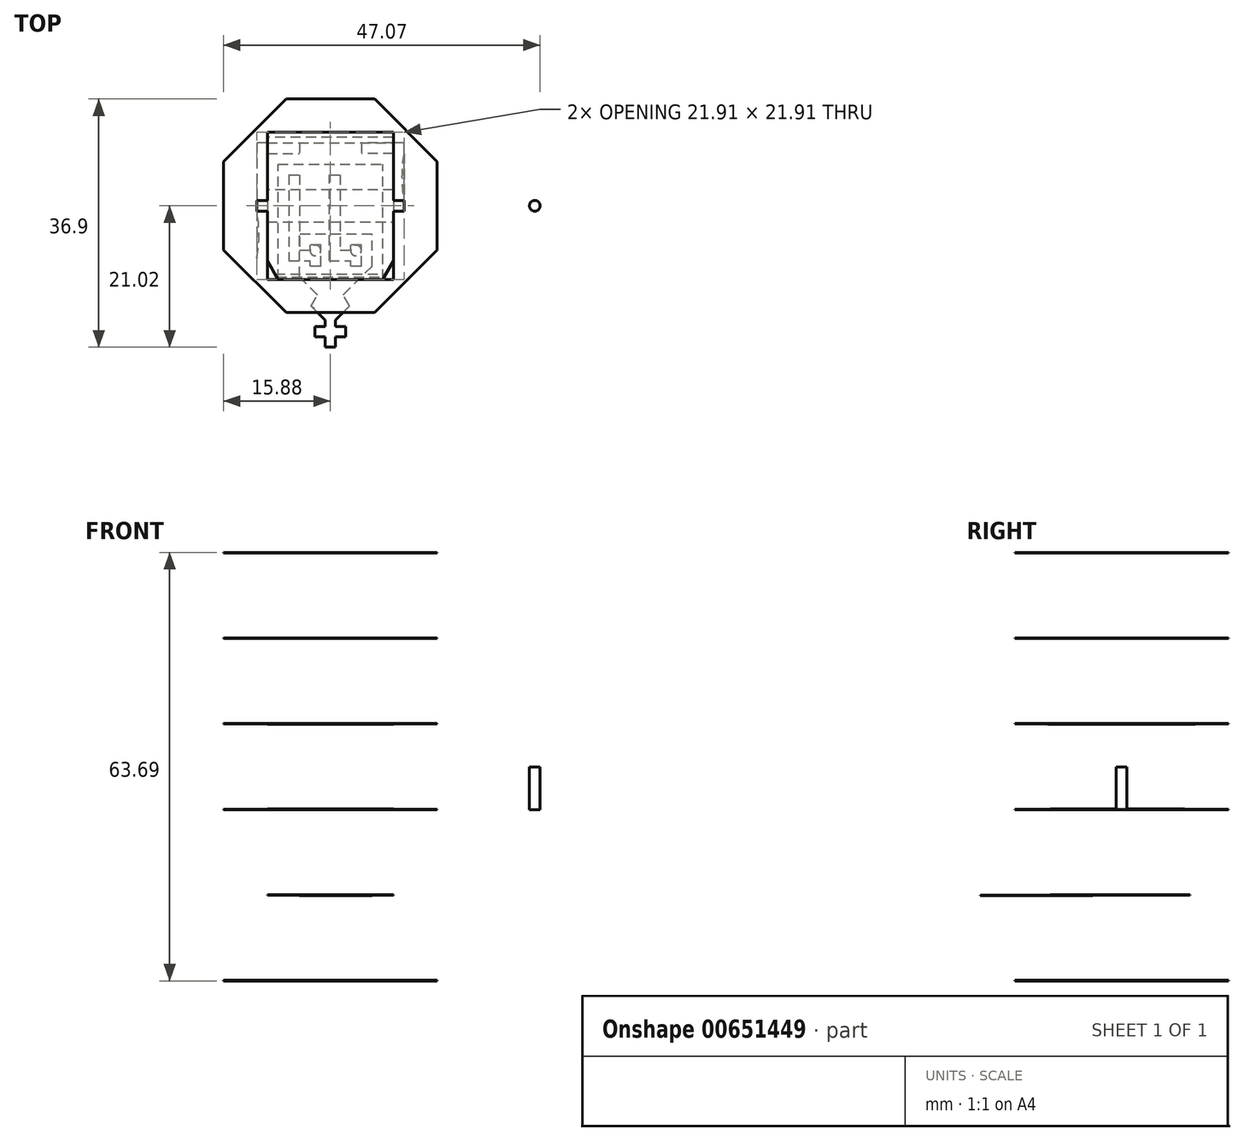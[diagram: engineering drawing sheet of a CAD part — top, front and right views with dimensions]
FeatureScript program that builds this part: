
annotation { "Feature Type Name" : "Feature", "Feature Type Description" : "" }
export const myFeature = defineFeature(function(context is Context, id is Id, definition is map)
    precondition{}
    {
        {
            assignVariable(context, id + "F0", {"name" : "h", "anyValue" : 1 / 16});
        }
        {
            var Q0;
            Q0=qCreatedBy(makeId("Top.planeOp"),FACE);
            var sketch = newSketch(context, id + "F1", { "sketchPlane" : qUnion([Q0])});
            skCircle(sketch, "E0.cCircle", {"center": v(0, 0) * mm, "radius": 15.88 * mm, "construction": true});
            skLineSegment(sketch, "E0.0", {"start": v(-6.58, 15.88) * mm, "end": v(6.58, 15.88) * mm});
            skLineSegment(sketch, "E0.1", {"start": v(6.58, 15.88) * mm, "end": v(15.88, 6.58) * mm});
            skLineSegment(sketch, "E0.2", {"start": v(15.88, 6.58) * mm, "end": v(15.88, -6.58) * mm});
            skLineSegment(sketch, "E0.3", {"start": v(15.88, -6.58) * mm, "end": v(6.58, -15.87) * mm});
            skLineSegment(sketch, "E0.4", {"start": v(6.58, -15.88) * mm, "end": v(-6.58, -15.88) * mm});
            skLineSegment(sketch, "E0.5", {"start": v(-6.58, -15.88) * mm, "end": v(-15.88, -6.58) * mm});
            skLineSegment(sketch, "E0.6", {"start": v(-15.87, -6.58) * mm, "end": v(-15.88, 6.58) * mm});
            skLineSegment(sketch, "E0.7", {"start": v(-15.88, 6.58) * mm, "end": v(-6.58, 15.88) * mm});
            skPoint(sketch, "E0.0.midPoint", {"position": v(0, 15.88) * mm});
            skLineSegment(sketch, "E1.bottom", {"start": v(9.37, 10.95) * mm, "end": v(-9.37, 10.95) * mm});
            skLineSegment(sketch, "E1.top", {"start": v(9.37, -10.95) * mm, "end": v(-9.37, -10.95) * mm});
            skLineSegment(sketch, "E1.left", {"start": v(9.37, 10.95) * mm, "end": v(9.37, -10.95) * mm});
            skLineSegment(sketch, "E1.right", {"start": v(-9.37, 10.95) * mm, "end": v(-9.37, -10.95) * mm});
            skSolve(sketch);
        }
        {
            var Q0;
            Q0=makeQuery(id+"F1.imprint","IMPRINT",FACE,{"disambiguationData":[TD([[makeQuery(id+"F1.imprint","IMPRINT",EDGE,{"derivedFrom":sQuery(id+"F1.wireOp",EDGE,"E0.0")}),-1.0]])]});
            extrude(context, id + "F2", {"entities" : qUnion([Q0]), "depth" : (getVariable(context, 'h')) * mm, "offsetDistance" : 25.4 * mm});
        }
        {
            var Q0;
            Q0=makeQuery(id+"F2.opExtrude","CAP_FACE",FACE,{"disambiguationData":[OSD([sQuery(id+"F1.wireOp",EDGE,"E0.0"),sQuery(id+"F1.wireOp",EDGE,"E0.1"),sQuery(id+"F1.wireOp",EDGE,"E0.2"),sQuery(id+"F1.wireOp",EDGE,"E0.3"),sQuery(id+"F1.wireOp",EDGE,"E0.4"),sQuery(id+"F1.wireOp",EDGE,"E0.5"),sQuery(id+"F1.wireOp",EDGE,"E0.6"),sQuery(id+"F1.wireOp",EDGE,"E0.7"),sQuery(id+"F1.wireOp",EDGE,"E1.bottom"),sQuery(id+"F1.wireOp",EDGE,"E1.top"),sQuery(id+"F1.wireOp",EDGE,"E1.left"),sQuery(id+"F1.wireOp",EDGE,"E1.right")])],"isStart":false});
            cPlane(context, id + "F3", {"entities" : qUnion([Q0]), "cplaneType" : CPlaneType.OFFSET, "offset" : 12.7 * mm, "width" : 152.4 * mm, "height" : 152.4 * mm});
        }
        {
            var Q0;
            Q0=qCreatedBy(id+"F3.planeOp",FACE);
            var sketch = newSketch(context, id + "F4", { "sketchPlane" : qUnion([Q0])});
            skLineSegment(sketch, "E2.0", {"start": v(-15.88, 6.58) * mm, "end": v(-6.58, 15.88) * mm});
            skLineSegment(sketch, "E3.0", {"start": v(-15.87, -6.58) * mm, "end": v(-15.88, 6.58) * mm});
            skLineSegment(sketch, "E4.0", {"start": v(-6.58, -15.88) * mm, "end": v(-15.88, -6.58) * mm});
            skLineSegment(sketch, "E5.0", {"start": v(6.58, -15.88) * mm, "end": v(-6.58, -15.88) * mm});
            skLineSegment(sketch, "E6.0", {"start": v(15.88, -6.58) * mm, "end": v(6.58, -15.88) * mm});
            skLineSegment(sketch, "E7.0", {"start": v(15.88, 6.58) * mm, "end": v(15.88, -6.58) * mm});
            skLineSegment(sketch, "E8.0", {"start": v(6.58, 15.88) * mm, "end": v(15.88, 6.58) * mm});
            skLineSegment(sketch, "E9.0", {"start": v(-6.58, 15.88) * mm, "end": v(6.58, 15.88) * mm});
            skLineSegment(sketch, "E10.bottom", {"start": v(10.95, 9.37) * mm, "end": v(-10.95, 9.37) * mm});
            skLineSegment(sketch, "E10.top", {"start": v(10.95, -9.37) * mm, "end": v(-10.95, -9.37) * mm});
            skLineSegment(sketch, "E10.left", {"start": v(10.95, 9.37) * mm, "end": v(10.95, -9.37) * mm});
            skLineSegment(sketch, "E10.right", {"start": v(-10.95, 9.37) * mm, "end": v(-10.95, -9.37) * mm});
            skPoint(sketch, "E10.middle", {"position": v(0, 0) * mm});
            skLineSegment(sketch, "E11.bottom", {"start": v(-9.37, 9.37) * mm, "end": v(9.37, 9.37) * mm});
            skLineSegment(sketch, "E11.top", {"start": v(-9.37, 10.95) * mm, "end": v(9.37, 10.95) * mm});
            skLineSegment(sketch, "E11.left", {"start": v(-9.37, 9.37) * mm, "end": v(-9.37, 10.95) * mm});
            skLineSegment(sketch, "E11.right", {"start": v(9.37, 9.37) * mm, "end": v(9.37, 10.95) * mm});
            skLineSegment(sketch, "E12.bottom", {"start": v(-9.37, -9.37) * mm, "end": v(9.37, -9.37) * mm});
            skLineSegment(sketch, "E12.top", {"start": v(-9.37, -10.95) * mm, "end": v(9.37, -10.95) * mm});
            skLineSegment(sketch, "E12.left", {"start": v(-9.37, -9.37) * mm, "end": v(-9.37, -10.95) * mm});
            skLineSegment(sketch, "E12.right", {"start": v(9.37, -9.37) * mm, "end": v(9.37, -10.95) * mm});
            skSolve(sketch);
        }
        {
            var Q0;
            Q0=makeQuery(id+"F4.imprint","IMPRINT",FACE,{"disambiguationData":[TD([[makeQuery(id+"F4.imprint","IMPRINT",EDGE,{"derivedFrom":sQuery(id+"F4.wireOp",EDGE,"E2.0")}),-1.0]])]});
            extrude(context, id + "F5", {"entities" : qUnion([Q0]), "depth" : (getVariable(context, 'h')) * mm, "offsetDistance" : 25.4 * mm});
        }
        {
            var Q0;
            Q0=makeQuery(id+"F2.opExtrude","CAP_FACE",FACE,{"disambiguationData":[OSD([sQuery(id+"F1.wireOp",EDGE,"E0.0"),sQuery(id+"F1.wireOp",EDGE,"E0.1"),sQuery(id+"F1.wireOp",EDGE,"E0.2"),sQuery(id+"F1.wireOp",EDGE,"E0.3"),sQuery(id+"F1.wireOp",EDGE,"E0.4"),sQuery(id+"F1.wireOp",EDGE,"E0.5"),sQuery(id+"F1.wireOp",EDGE,"E0.6"),sQuery(id+"F1.wireOp",EDGE,"E0.7"),sQuery(id+"F1.wireOp",EDGE,"E1.bottom"),sQuery(id+"F1.wireOp",EDGE,"E1.top"),sQuery(id+"F1.wireOp",EDGE,"E1.left"),sQuery(id+"F1.wireOp",EDGE,"E1.right")])],"isStart":false});
            var sketch = newSketch(context, id + "F6", { "sketchPlane" : qUnion([Q0])});
            skLineSegment(sketch, "E13.bottom", {"start": v(-9.37, 9.37) * mm, "end": v(9.37, 9.37) * mm});
            skLineSegment(sketch, "E13.top", {"start": v(-9.37, -10.16) * mm, "end": v(9.37, -10.16) * mm});
            skLineSegment(sketch, "E13.left", {"start": v(-9.37, 9.37) * mm, "end": v(-9.37, -10.16) * mm});
            skLineSegment(sketch, "E13.right", {"start": v(9.37, 9.37) * mm, "end": v(9.37, -10.16) * mm});
            skLineSegment(sketch, "E14.bottom", {"start": v(9.37, 9.37) * mm, "end": v(-9.37, 9.37) * mm});
            skLineSegment(sketch, "E14.top", {"start": v(9.37, 10.16) * mm, "end": v(-9.37, 10.16) * mm});
            skLineSegment(sketch, "E14.left", {"start": v(9.37, 9.37) * mm, "end": v(9.37, 10.16) * mm});
            skLineSegment(sketch, "E14.right", {"start": v(-9.37, 9.37) * mm, "end": v(-9.37, 10.16) * mm});
            skLineSegment(sketch, "E15.top", {"start": v(-9.37, -10.56) * mm, "end": v(9.37, -10.56) * mm});
            skLineSegment(sketch, "E15.left", {"start": v(-9.37, -10.16) * mm, "end": v(-9.37, -10.56) * mm});
            skLineSegment(sketch, "E15.right", {"start": v(9.37, -10.16) * mm, "end": v(9.37, -10.56) * mm});
            skSolve(sketch);
        }
        {
            var Q0;
            Q0=makeQuery(id+"F6.imprint","IMPRINT",FACE,{"disambiguationData":[TD([[makeQuery(id+"F6.imprint","IMPRINT",EDGE,{"derivedFrom":sQuery(id+"F6.wireOp",EDGE,"E13.left")}),1.0]])]});
            var Q1;
            Q1=makeQuery(id+"F6.imprint","IMPRINT",FACE,{"disambiguationData":[TD([[makeQuery(id+"F6.imprint","IMPRINT",EDGE,{"derivedFrom":sQuery(id+"F6.wireOp",EDGE,"E14.bottom")}),-1.0]])]});
            var Q2;
            Q2=makeQuery(id+"F6.imprint","IMPRINT",FACE,{"disambiguationData":[TD([[makeQuery(id+"F6.imprint","IMPRINT",EDGE,{"derivedFrom":sQuery(id+"F6.wireOp",EDGE,"E13.top")}),-1.0]])]});
            extrude(context, id + "F7", {"entities" : qUnion([Q0, Q1, Q2]), "depth" : (getVariable(context, 'h')) * mm, "offsetDistance" : 25.4 * mm});
        }
        {
            var Q0;
            Q0=makeQuery(id+"F5.opExtrude","CAP_FACE",FACE,{"disambiguationData":[OSD([sQuery(id+"F4.wireOp",EDGE,"E2.0"),sQuery(id+"F4.wireOp",EDGE,"E3.0"),sQuery(id+"F4.wireOp",EDGE,"E4.0"),sQuery(id+"F4.wireOp",EDGE,"E5.0"),sQuery(id+"F4.wireOp",EDGE,"E6.0"),sQuery(id+"F4.wireOp",EDGE,"E7.0"),sQuery(id+"F4.wireOp",EDGE,"E8.0"),sQuery(id+"F4.wireOp",EDGE,"E9.0"),sQuery(id+"F4.wireOp",EDGE,"E10.bottom"),sQuery(id+"F4.wireOp",EDGE,"E10.top"),sQuery(id+"F4.wireOp",EDGE,"E10.left"),sQuery(id+"F4.wireOp",EDGE,"E10.right"),sQuery(id+"F4.wireOp",EDGE,"E11.top"),sQuery(id+"F4.wireOp",EDGE,"E11.left"),sQuery(id+"F4.wireOp",EDGE,"E11.right"),sQuery(id+"F4.wireOp",EDGE,"E12.top"),sQuery(id+"F4.wireOp",EDGE,"E12.left"),sQuery(id+"F4.wireOp",EDGE,"E12.right")])],"isStart":true});
            var sketch = newSketch(context, id + "F8", { "sketchPlane" : qUnion([Q0])});
            skLineSegment(sketch, "E16.bottom", {"start": v(-9.37, -10.95) * mm, "end": v(9.37, -10.95) * mm});
            skLineSegment(sketch, "E16.top", {"start": v(-9.37, 10.95) * mm, "end": v(9.37, 10.95) * mm});
            skLineSegment(sketch, "E16.left", {"start": v(-9.37, -10.95) * mm, "end": v(-9.37, 10.95) * mm});
            skLineSegment(sketch, "E16.right", {"start": v(9.37, -10.95) * mm, "end": v(9.37, 10.95) * mm});
            skLineSegment(sketch, "E17.bottom", {"start": v(-9.37, -9.37) * mm, "end": v(-4.6, -9.37) * mm});
            skLineSegment(sketch, "E17.top", {"start": v(-9.37, -7.78) * mm, "end": v(-4.6, -7.78) * mm});
            skLineSegment(sketch, "E17.left", {"start": v(-9.37, -9.37) * mm, "end": v(-9.37, -7.78) * mm});
            skLineSegment(sketch, "E17.right", {"start": v(-4.6, -9.37) * mm, "end": v(-4.6, -7.78) * mm});
            skLineSegment(sketch, "E18.bottom", {"start": v(9.37, -9.37) * mm, "end": v(4.6, -9.37) * mm});
            skLineSegment(sketch, "E18.top", {"start": v(9.37, -7.78) * mm, "end": v(4.6, -7.78) * mm});
            skLineSegment(sketch, "E18.left", {"start": v(9.37, -9.37) * mm, "end": v(9.37, -7.78) * mm});
            skLineSegment(sketch, "E18.right", {"start": v(4.6, -9.37) * mm, "end": v(4.6, -7.78) * mm});
            skSolve(sketch);
        }
        {
            var Q0;
            {var subQ12=sQuery(id+"F8.wireOp",EDGE,"E16.bottom");Q0=makeQuery(id+"F8.imprint","IMPRINT",FACE,{"disambiguationData":[TD([[makeQuery(id+"F8.imprint","IMPRINT",EDGE,{"derivedFrom":subQ12}),1.0]])]});}
            extrude(context, id + "F9", {"entities" : qUnion([Q0]), "depth" : (getVariable(context, 'h')) * mm, "offsetDistance" : 25.4 * mm});
        }
        {
            var Q0;
            Q0=makeQuery(id+"F5.opExtrude","CAP_FACE",FACE,{"disambiguationData":[OSD([sQuery(id+"F4.wireOp",EDGE,"E2.0"),sQuery(id+"F4.wireOp",EDGE,"E3.0"),sQuery(id+"F4.wireOp",EDGE,"E4.0"),sQuery(id+"F4.wireOp",EDGE,"E5.0"),sQuery(id+"F4.wireOp",EDGE,"E6.0"),sQuery(id+"F4.wireOp",EDGE,"E7.0"),sQuery(id+"F4.wireOp",EDGE,"E8.0"),sQuery(id+"F4.wireOp",EDGE,"E9.0"),sQuery(id+"F4.wireOp",EDGE,"E10.bottom"),sQuery(id+"F4.wireOp",EDGE,"E10.top"),sQuery(id+"F4.wireOp",EDGE,"E10.left"),sQuery(id+"F4.wireOp",EDGE,"E10.right"),sQuery(id+"F4.wireOp",EDGE,"E11.top"),sQuery(id+"F4.wireOp",EDGE,"E11.left"),sQuery(id+"F4.wireOp",EDGE,"E11.right"),sQuery(id+"F4.wireOp",EDGE,"E12.top"),sQuery(id+"F4.wireOp",EDGE,"E12.left"),sQuery(id+"F4.wireOp",EDGE,"E12.right")])],"isStart":false});
            var sketch = newSketch(context, id + "F10", { "sketchPlane" : qUnion([Q0])});
            skArc(sketch, "E19", {"start": v(-10.95, 0.8) * mm, "mid": v(-10.62, 4.29) * mm, "end": v(-10.95, 7.78) * mm});
            skArc(sketch, "E20.MirrorCS", {"start": v(10.95, 0.8) * mm, "mid": v(10.62, 4.29) * mm, "end": v(10.95, 7.78) * mm});
            skArc(sketch, "E21.MirrorCS", {"start": v(-10.95, -0.8) * mm, "mid": v(-10.62, -4.29) * mm, "end": v(-10.95, -7.78) * mm});
            skArc(sketch, "E22.MirrorCS", {"start": v(10.95, -0.8) * mm, "mid": v(10.62, -4.29) * mm, "end": v(10.95, -7.78) * mm});
            skSolve(sketch);
        }
        {
            var Q0;
            {var subQ0=sQuery(id+"F10.wireOp",EDGE,"E19");Q0=makeQuery(id+"F10.imprint","IMPRINT",FACE,{"disambiguationData":[TD([[makeQuery(id+"F10.imprint","IMPRINT",EDGE,{"derivedFrom":subQ0}),1.0]])]});}
            var Q1;
            {var subQ0=sQuery(id+"F10.wireOp",EDGE,"E20.MirrorCS");Q1=makeQuery(id+"F10.imprint","IMPRINT",FACE,{"disambiguationData":[TD([[makeQuery(id+"F10.imprint","IMPRINT",EDGE,{"derivedFrom":subQ0}),-1.0]])]});}
            var Q2;
            {var subQ0=sQuery(id+"F10.wireOp",EDGE,"E21.MirrorCS");Q2=makeQuery(id+"F10.imprint","IMPRINT",FACE,{"disambiguationData":[TD([[makeQuery(id+"F10.imprint","IMPRINT",EDGE,{"derivedFrom":subQ0}),-1.0]])]});}
            var Q3;
            {var subQ0=sQuery(id+"F10.wireOp",EDGE,"E22.MirrorCS");Q3=makeQuery(id+"F10.imprint","IMPRINT",FACE,{"disambiguationData":[TD([[makeQuery(id+"F10.imprint","IMPRINT",EDGE,{"derivedFrom":subQ0}),1.0]])]});}
            extrude(context, id + "F11", {"entities" : qUnion([Q0, Q1, Q2, Q3]), "operationType" : NewBodyOperationType.ADD, "oppositeDirection" : true, "depth" : (getVariable(context, 'h')) * mm, "offsetDistance" : 25.4 * mm});
        }
        {
            var Q0;
            Q0=qCreatedBy(id+"F3.planeOp",FACE);
            cPlane(context, id + "F12", {"entities" : qUnion([Q0]), "cplaneType" : CPlaneType.OFFSET, "offset" : 12.7 * mm, "width" : 150 * mm, "height" : 150 * mm});
        }
        {
            var Q0;
            Q0=qCreatedBy(id+"F12.planeOp",FACE);
            var sketch = newSketch(context, id + "F13", { "sketchPlane" : qUnion([Q0])});
            skLineSegment(sketch, "E23.0", {"start": v(-6.58, 15.88) * mm, "end": v(6.58, 15.88) * mm});
            skLineSegment(sketch, "E24.0", {"start": v(-15.88, 6.58) * mm, "end": v(-6.58, 15.88) * mm});
            skLineSegment(sketch, "E25.0", {"start": v(-15.87, -6.58) * mm, "end": v(-15.88, 6.58) * mm});
            skLineSegment(sketch, "E26.0", {"start": v(-6.58, -15.88) * mm, "end": v(-15.88, -6.58) * mm});
            skLineSegment(sketch, "E27.0", {"start": v(6.58, -15.88) * mm, "end": v(-6.58, -15.88) * mm});
            skLineSegment(sketch, "E28.0", {"start": v(15.88, -6.58) * mm, "end": v(6.58, -15.88) * mm});
            skLineSegment(sketch, "E29.0", {"start": v(15.88, 6.58) * mm, "end": v(15.88, -6.58) * mm});
            skLineSegment(sketch, "E30.0", {"start": v(6.58, 15.88) * mm, "end": v(15.88, 6.58) * mm});
            skLineSegment(sketch, "E31.0", {"start": v(-9.37, 10.95) * mm, "end": v(9.37, 10.95) * mm});
            skLineSegment(sketch, "E32.0", {"start": v(-9.37, 9.37) * mm, "end": v(-9.37, 10.95) * mm});
            skLineSegment(sketch, "E33.0", {"start": v(-9.37, 9.37) * mm, "end": v(-10.95, 9.37) * mm});
            skLineSegment(sketch, "E34.0", {"start": v(9.37, 9.37) * mm, "end": v(9.37, 10.95) * mm});
            skLineSegment(sketch, "E35.0", {"start": v(10.95, 9.37) * mm, "end": v(9.37, 9.37) * mm});
            skLineSegment(sketch, "E36", {"start": v(-10.95, 9.37) * mm, "end": v(-10.95, -0.8) * mm});
            skLineSegment(sketch, "E37", {"start": v(-10.95, -0.8) * mm, "end": v(10.95, -0.8) * mm});
            skLineSegment(sketch, "E38", {"start": v(10.95, -0.8) * mm, "end": v(10.95, 9.37) * mm});
            skLineSegment(sketch, "E39.bottom", {"start": v(-9.37, -0.8) * mm, "end": v(9.37, -0.8) * mm});
            skLineSegment(sketch, "E39.top", {"start": v(-9.37, -10.95) * mm, "end": v(9.37, -10.95) * mm});
            skLineSegment(sketch, "E39.left", {"start": v(-9.37, -0.8) * mm, "end": v(-9.37, -10.95) * mm});
            skLineSegment(sketch, "E39.right", {"start": v(9.37, -0.8) * mm, "end": v(9.37, -10.95) * mm});
            skSolve(sketch);
        }
        {
            var Q0;
            Q0=makeQuery(id+"F13.imprint","IMPRINT",FACE,{"disambiguationData":[TD([[makeQuery(id+"F13.imprint","IMPRINT",EDGE,{"derivedFrom":sQuery(id+"F13.wireOp",EDGE,"E23.0")}),-1.0]])]});
            extrude(context, id + "F14", {"entities" : qUnion([Q0]), "depth" : (getVariable(context, 'h')) * mm, "offsetDistance" : 25.4 * mm});
        }
        {
            var Q0;
            Q0=qCreatedBy(id+"F12.planeOp",FACE);
            cPlane(context, id + "F15", {"entities" : qUnion([Q0]), "cplaneType" : CPlaneType.OFFSET, "offset" : 12.7 * mm, "width" : 152.4 * mm, "height" : 152.4 * mm});
        }
        {
            var Q0;
            Q0=qCreatedBy(id+"F15.planeOp",FACE);
            var sketch = newSketch(context, id + "F16", { "sketchPlane" : qUnion([Q0])});
            skLineSegment(sketch, "E40.0", {"start": v(-15.88, 6.58) * mm, "end": v(-6.58, 15.88) * mm});
            skLineSegment(sketch, "E41.0", {"start": v(-6.58, 15.88) * mm, "end": v(6.58, 15.88) * mm});
            skLineSegment(sketch, "E42.0", {"start": v(6.58, 15.88) * mm, "end": v(15.88, 6.58) * mm});
            skLineSegment(sketch, "E43.0", {"start": v(15.88, 6.58) * mm, "end": v(15.88, -6.58) * mm});
            skLineSegment(sketch, "E44.0", {"start": v(15.88, -6.58) * mm, "end": v(6.58, -15.88) * mm});
            skLineSegment(sketch, "E45.0", {"start": v(6.58, -15.88) * mm, "end": v(-6.58, -15.88) * mm});
            skLineSegment(sketch, "E46.0", {"start": v(-6.58, -15.88) * mm, "end": v(-15.88, -6.58) * mm});
            skLineSegment(sketch, "E47.0", {"start": v(-15.87, -6.58) * mm, "end": v(-15.88, 6.58) * mm});
            skLineSegment(sketch, "E48.0", {"start": v(9.37, 10.95) * mm, "end": v(-9.37, 10.95) * mm});
            skLineSegment(sketch, "E49.0", {"start": v(9.37, 10.95) * mm, "end": v(9.37, -10.95) * mm});
            skLineSegment(sketch, "E50.0", {"start": v(-9.37, 10.95) * mm, "end": v(-9.37, -10.95) * mm});
            skLineSegment(sketch, "E51.0", {"start": v(9.37, -10.95) * mm, "end": v(-9.37, -10.95) * mm});
            skLineSegment(sketch, "E52.bottom", {"start": v(-9.37, 0.8) * mm, "end": v(-10.95, 0.8) * mm});
            skLineSegment(sketch, "E52.top", {"start": v(-9.37, -0.8) * mm, "end": v(-10.95, -0.8) * mm});
            skLineSegment(sketch, "E52.left", {"start": v(-9.37, 0.8) * mm, "end": v(-9.37, -0.8) * mm});
            skLineSegment(sketch, "E52.right", {"start": v(-10.95, 0.8) * mm, "end": v(-10.95, -0.8) * mm});
            skPoint(sketch, "E52.middle", {"position": v(-10.16, 0) * mm});
            skLineSegment(sketch, "E53.bottom", {"start": v(9.37, 0.8) * mm, "end": v(10.95, 0.8) * mm});
            skLineSegment(sketch, "E53.top", {"start": v(9.37, -0.8) * mm, "end": v(10.95, -0.8) * mm});
            skLineSegment(sketch, "E53.left", {"start": v(9.37, 0.8) * mm, "end": v(9.37, -0.8) * mm});
            skLineSegment(sketch, "E53.right", {"start": v(10.95, 0.8) * mm, "end": v(10.95, -0.8) * mm});
            skPoint(sketch, "E53.middle", {"position": v(10.16, 0) * mm});
            skSolve(sketch);
        }
        {
            var Q0;
            Q0=makeQuery(id+"F16.imprint","IMPRINT",FACE,{"disambiguationData":[TD([[makeQuery(id+"F16.imprint","IMPRINT",EDGE,{"derivedFrom":sQuery(id+"F16.wireOp",EDGE,"E40.0")}),-1.0]])]});
            extrude(context, id + "F17", {"entities" : qUnion([Q0]), "depth" : (getVariable(context, 'h')) * mm, "offsetDistance" : 25.4 * mm});
        }
        {
            var Q0;
            Q0=qCreatedBy(makeId("Top.planeOp"),FACE);
            cPlane(context, id + "F18", {"entities" : qUnion([Q0]), "cplaneType" : CPlaneType.OFFSET, "offset" : 12.7 * mm, "oppositeDirection" : true, "width" : 152.4 * mm, "height" : 152.4 * mm});
        }
        {
            var Q0;
            Q0=qCreatedBy(id+"F18.planeOp",FACE);
            var sketch = newSketch(context, id + "F19", { "sketchPlane" : qUnion([Q0])});
            skLineSegment(sketch, "E54.bottom", {"start": v(-6.2, 4.6) * mm, "end": v(-4.6, 4.6) * mm});
            skLineSegment(sketch, "E54.top", {"start": v(-6.2, -8.18) * mm, "end": v(-4.6, -8.18) * mm});
            skLineSegment(sketch, "E54.left", {"start": v(-6.2, 4.6) * mm, "end": v(-6.2, -8.18) * mm});
            skLineSegment(sketch, "E54.right", {"start": v(-4.6, 4.6) * mm, "end": v(-4.6, -8.18) * mm});
            skLineSegment(sketch, "E55.bottom", {"start": v(-6.2, -8.18) * mm, "end": v(-1.43, -8.18) * mm});
            skLineSegment(sketch, "E55.top", {"start": v(-6.2, -6.59) * mm, "end": v(-1.43, -6.59) * mm});
            skLineSegment(sketch, "E55.left", {"start": v(-6.2, -8.18) * mm, "end": v(-6.2, -6.59) * mm});
            skLineSegment(sketch, "E55.right", {"start": v(-1.43, -8.18) * mm, "end": v(-1.43, -6.59) * mm});
            skLineSegment(sketch, "E56.bottom", {"start": v(-1.43, -8.97) * mm, "end": v(-3.02, -8.97) * mm});
            skLineSegment(sketch, "E56.top", {"start": v(-1.43, -5.8) * mm, "end": v(-3.02, -5.8) * mm});
            skLineSegment(sketch, "E56.left", {"start": v(-1.43, -8.97) * mm, "end": v(-1.43, -5.8) * mm});
            skLineSegment(sketch, "E56.right", {"start": v(-3.02, -8.97) * mm, "end": v(-3.02, -5.8) * mm});
            skLineSegment(sketch, "E57.0.0", {"start": v(-9.37, 10.16) * mm, "end": v(-9.37, -10.56) * mm});
            skLineSegment(sketch, "E57.0.1", {"start": v(-9.37, -10.56) * mm, "end": v(9.37, -10.56) * mm});
            skLineSegment(sketch, "E57.0.2", {"start": v(9.37, -10.56) * mm, "end": v(9.37, 10.16) * mm});
            skLineSegment(sketch, "E57.0.3", {"start": v(9.37, 10.16) * mm, "end": v(-9.37, 10.16) * mm});
            skLineSegment(sketch, "E58.1.0.0", {"start": v(-0.15, 4.6) * mm, "end": v(1.44, 4.6) * mm});
            skLineSegment(sketch, "E58.1.0.1", {"start": v(4.62, -8.97) * mm, "end": v(3.03, -8.97) * mm});
            skLineSegment(sketch, "E58.1.0.2", {"start": v(-0.15, -6.59) * mm, "end": v(4.62, -6.59) * mm});
            skLineSegment(sketch, "E58.1.0.3", {"start": v(4.62, -5.8) * mm, "end": v(3.03, -5.8) * mm});
            skLineSegment(sketch, "E58.1.0.4", {"start": v(3.03, -8.97) * mm, "end": v(3.03, -5.8) * mm});
            skLineSegment(sketch, "E58.1.0.5", {"start": v(-0.15, -8.18) * mm, "end": v(-0.15, -6.59) * mm});
            skLineSegment(sketch, "E58.1.0.6", {"start": v(1.44, 4.6) * mm, "end": v(1.44, -8.18) * mm});
            skLineSegment(sketch, "E58.1.0.7", {"start": v(4.62, -8.97) * mm, "end": v(4.62, -5.8) * mm});
            skLineSegment(sketch, "E58.1.0.8", {"start": v(-0.15, -8.18) * mm, "end": v(4.62, -8.18) * mm});
            skLineSegment(sketch, "E58.1.0.9", {"start": v(-0.15, 4.6) * mm, "end": v(-0.15, -8.18) * mm});
            skLineSegment(sketch, "E58.1.0.10", {"start": v(4.62, -8.18) * mm, "end": v(4.62, -6.59) * mm});
            skLineSegment(sketch, "E58.1.0.11", {"start": v(-0.15, -8.18) * mm, "end": v(1.44, -8.18) * mm});
            skLineSegment(sketch, "E58.direction1", {"start": v(-6.2, -8.18) * mm, "end": v(-0.15, -8.18) * mm, "construction": true});
            skSolve(sketch);
        }
        {
            var Q0;
            {var subQ10=sQuery(id+"F19.wireOp",EDGE,"E54.bottom");Q0=makeQuery(id+"F19.imprint","IMPRINT",FACE,{"disambiguationData":[TD([[makeQuery(id+"F19.imprint","IMPRINT",EDGE,{"derivedFrom":subQ10}),1.0]])]});}
            extrude(context, id + "F20", {"entities" : qUnion([Q0]), "depth" : (getVariable(context, 'h')) * mm, "offsetDistance" : 25.4 * mm});
        }
        {
            var Q0;
            Q0=qCreatedBy(makeId("Top.planeOp"),FACE);
            cPlane(context, id + "F21", {"entities" : qUnion([Q0]), "cplaneType" : CPlaneType.OFFSET, "offset" : 25.4 * mm, "oppositeDirection" : true, "width" : 152.4 * mm, "height" : 152.4 * mm});
        }
        {
            var Q0;
            Q0=qCreatedBy(id+"F21.planeOp",FACE);
            var sketch = newSketch(context, id + "F22", { "sketchPlane" : qUnion([Q0])});
            skLineSegment(sketch, "E59.0", {"start": v(-6.58, 15.88) * mm, "end": v(6.58, 15.88) * mm});
            skLineSegment(sketch, "E60.0", {"start": v(-15.88, 6.58) * mm, "end": v(-6.58, 15.88) * mm});
            skLineSegment(sketch, "E61.0", {"start": v(-15.87, -6.58) * mm, "end": v(-15.88, 6.58) * mm});
            skLineSegment(sketch, "E62.0", {"start": v(-6.58, -15.88) * mm, "end": v(-15.88, -6.58) * mm});
            skLineSegment(sketch, "E63.0", {"start": v(6.58, -15.88) * mm, "end": v(-6.58, -15.88) * mm});
            skLineSegment(sketch, "E64.0", {"start": v(15.88, -6.58) * mm, "end": v(6.58, -15.87) * mm});
            skLineSegment(sketch, "E65.0", {"start": v(15.88, 6.58) * mm, "end": v(15.88, -6.58) * mm});
            skLineSegment(sketch, "E66.0", {"start": v(6.58, 15.88) * mm, "end": v(15.88, 6.58) * mm});
            skSolve(sketch);
        }
        {
            var Q0;
            Q0=makeQuery(id+"F22.imprint","IMPRINT",FACE,{"disambiguationData":[TD([[makeQuery(id+"F22.imprint","IMPRINT",EDGE,{"derivedFrom":sQuery(id+"F22.wireOp",EDGE,"E59.0")}),-1.0]])]});
            extrude(context, id + "F23", {"entities" : qUnion([Q0]), "depth" : (getVariable(context, 'h')) * mm, "offsetDistance" : 25.4 * mm});
        }
        {
            var Q0;
            Q0=makeQuery(id+"F6.imprint","IMPRINT",FACE,{"disambiguationData":[TD([[makeQuery(id+"F6.imprint","IMPRINT",EDGE,{"derivedFrom":sQuery(id+"F6.wireOp",EDGE,"E13.left")}),1.0]])]});
            extrude(context, id + "F24", {"entities" : qUnion([Q0]), "oppositeDirection" : true, "depth" : (getVariable(context, 'h')) * mm, "offsetDistance" : 25.4 * mm});
        }
        {
            var Q0;
            Q0=makeQuery(id+"F9.opExtrude","CAP_FACE",FACE,{"disambiguationData":[OSD([sQuery(id+"F8.wireOp",EDGE,"E16.bottom"),sQuery(id+"F8.wireOp",EDGE,"E16.top"),sQuery(id+"F8.wireOp",EDGE,"E16.left"),sQuery(id+"F8.wireOp",EDGE,"E16.right"),sQuery(id+"F8.wireOp",EDGE,"E17.bottom"),sQuery(id+"F8.wireOp",EDGE,"E17.top"),sQuery(id+"F8.wireOp",EDGE,"E17.right"),sQuery(id+"F8.wireOp",EDGE,"E18.bottom"),sQuery(id+"F8.wireOp",EDGE,"E18.top"),sQuery(id+"F8.wireOp",EDGE,"E18.right")])],"isStart":false});
            var sketch = newSketch(context, id + "F25", { "sketchPlane" : qUnion([Q0])});
            skPoint(sketch, "E67.oppositeSnap0", {"position": v(7.78, -7.78) * mm});
            skLineSegment(sketch, "E67.bottom", {"start": v(-7.78, 10.95) * mm, "end": v(7.78, 10.95) * mm});
            skLineSegment(sketch, "E67.top", {"start": v(-7.78, -6.2) * mm, "end": v(7.78, -6.2) * mm});
            skLineSegment(sketch, "E67.left", {"start": v(-7.78, 10.95) * mm, "end": v(-7.78, -6.2) * mm});
            skLineSegment(sketch, "E67.right", {"start": v(7.78, 10.95) * mm, "end": v(7.78, -6.2) * mm});
            skSolve(sketch);
        }
        {
            var Q0;
            Q0=makeQuery(id+"F25.imprint","IMPRINT",FACE,{"disambiguationData":[TD([[makeQuery(id+"F25.imprint","IMPRINT",EDGE,{"derivedFrom":sQuery(id+"F25.wireOp",EDGE,"E67.bottom")}),-1.0]])]});
            extrude(context, id + "F26", {"entities" : qUnion([Q0]), "operationType" : NewBodyOperationType.REMOVE, "oppositeDirection" : true, "depth" : (getVariable(context, 'h')) * mm, "offsetDistance" : 25.4 * mm});
        }
        {
            var Q0;
            Q0=qCreatedBy(makeId("Top.planeOp"),FACE);
            var sketch = newSketch(context, id + "F27", { "sketchPlane" : qUnion([Q0])});
            skCircle(sketch, "E68", {"center": v(30.4, 0) * mm, "radius": 0.8 * mm});
            skSolve(sketch);
        }
        {
            var Q0;
            Q0=makeQuery(id+"F27.imprint","IMPRINT",FACE,{"disambiguationData":[TD([[makeQuery(id+"F27.imprint","IMPRINT",EDGE,{"derivedFrom":sQuery(id+"F27.wireOp",EDGE,"E68")}),1.0]])]});
            extrude(context, id + "F28", {"entities" : qUnion([Q0]), "depth" : 6.35 * mm, "offsetDistance" : 25.4 * mm});
        }
        {
            var Q0;
            Q0=makeQuery(id+"F23.opExtrude","CAP_FACE",FACE,{"disambiguationData":[OSD([sQuery(id+"F22.wireOp",EDGE,"E59.0"),sQuery(id+"F22.wireOp",EDGE,"E60.0"),sQuery(id+"F22.wireOp",EDGE,"E61.0"),sQuery(id+"F22.wireOp",EDGE,"E62.0"),sQuery(id+"F22.wireOp",EDGE,"E63.0"),sQuery(id+"F22.wireOp",EDGE,"E64.0"),sQuery(id+"F22.wireOp",EDGE,"E65.0"),sQuery(id+"F22.wireOp",EDGE,"E66.0")])],"isStart":true});
            var sketch = newSketch(context, id + "F29", { "sketchPlane" : qUnion([Q0])});
            skLineSegment(sketch, "E69.0.0", {"start": v(6.58, -15.88) * mm, "end": v(15.88, -6.58) * mm});
            skLineSegment(sketch, "E69.0.1", {"start": v(15.88, -6.58) * mm, "end": v(15.88, 6.58) * mm});
            skLineSegment(sketch, "E69.0.2", {"start": v(15.88, 6.58) * mm, "end": v(6.58, 15.88) * mm});
            skLineSegment(sketch, "E69.0.3", {"start": v(6.58, 15.88) * mm, "end": v(-6.58, 15.88) * mm});
            skLineSegment(sketch, "E69.0.4", {"start": v(-6.58, 15.88) * mm, "end": v(-15.88, 6.58) * mm});
            skLineSegment(sketch, "E69.0.5", {"start": v(-15.87, 6.58) * mm, "end": v(-15.88, -6.58) * mm});
            skLineSegment(sketch, "E69.0.6", {"start": v(-15.88, -6.58) * mm, "end": v(-6.58, -15.88) * mm});
            skLineSegment(sketch, "E69.0.7", {"start": v(-6.58, -15.88) * mm, "end": v(6.58, -15.88) * mm});
            skLineSegment(sketch, "E70.0", {"start": v(9.37, 10.95) * mm, "end": v(-9.37, 10.95) * mm});
            skLineSegment(sketch, "E71.0", {"start": v(-9.37, -10.95) * mm, "end": v(-9.37, 10.95) * mm});
            skLineSegment(sketch, "E72.0", {"start": v(9.37, -10.95) * mm, "end": v(9.37, 10.95) * mm});
            skLineSegment(sketch, "E73.0", {"start": v(9.37, -10.95) * mm, "end": v(-9.37, -10.95) * mm});
            skLineSegment(sketch, "E74", {"start": v(-9.37, 2.38) * mm, "end": v(9.37, 2.38) * mm});
            skLineSegment(sketch, "E75", {"start": v(9.37, -2.38) * mm, "end": v(-9.37, -2.38) * mm});
            skSolve(sketch);
        }
        {
            var Q0;
            {var subQ0=sQuery(id+"F29.wireOp",EDGE,"E70.0");Q0=makeQuery(id+"F29.imprint","IMPRINT",FACE,{"disambiguationData":[TD([[makeQuery(id+"F29.imprint","IMPRINT",EDGE,{"derivedFrom":subQ0}),1.0]])]});}
            var Q1;
            Q1=makeQuery(id+"F29.imprint","IMPRINT",FACE,{"disambiguationData":[TD([[makeQuery(id+"F29.imprint","IMPRINT",EDGE,{"derivedFrom":sQuery(id+"F29.wireOp",EDGE,"E69.0.0")}),1.0]])]});
            var Q2;
            {var subQ0=sQuery(id+"F29.wireOp",EDGE,"E73.0");Q2=makeQuery(id+"F29.imprint","IMPRINT",FACE,{"disambiguationData":[TD([[makeQuery(id+"F29.imprint","IMPRINT",EDGE,{"derivedFrom":subQ0}),-1.0]])]});}
            extrude(context, id + "F30", {"entities" : qUnion([Q0, Q1, Q2]), "depth" : (getVariable(context, 'h')) * mm, "offsetDistance" : 25.4 * mm});
        }
        {
            var Q0;
            Q0=makeQuery(id+"F9.opExtrude","CAP_FACE",FACE,{"disambiguationData":[OSD([sQuery(id+"F8.wireOp",EDGE,"E16.bottom"),sQuery(id+"F8.wireOp",EDGE,"E16.top"),sQuery(id+"F8.wireOp",EDGE,"E16.left"),sQuery(id+"F8.wireOp",EDGE,"E16.right"),sQuery(id+"F8.wireOp",EDGE,"E17.bottom"),sQuery(id+"F8.wireOp",EDGE,"E17.top"),sQuery(id+"F8.wireOp",EDGE,"E17.right"),sQuery(id+"F8.wireOp",EDGE,"E18.bottom"),sQuery(id+"F8.wireOp",EDGE,"E18.top"),sQuery(id+"F8.wireOp",EDGE,"E18.right")])],"isStart":false});
            var sketch = newSketch(context, id + "F31", { "sketchPlane" : qUnion([Q0])});
            skLineSegment(sketch, "E76", {"start": v(-9.37, 10.95) * mm, "end": v(-9.37, 8.2) * mm});
            skLineSegment(sketch, "E77", {"start": v(-9.37, 8.2) * mm, "end": v(-7.78, 10.95) * mm});
            skLineSegment(sketch, "E78", {"start": v(-7.78, 10.95) * mm, "end": v(-9.37, 10.95) * mm});
            skLineSegment(sketch, "E79.MirrorCS", {"start": v(9.37, 10.95) * mm, "end": v(9.37, 8.2) * mm});
            skLineSegment(sketch, "E80.MirrorCS", {"start": v(9.37, 8.2) * mm, "end": v(7.78, 10.95) * mm});
            skLineSegment(sketch, "E81.MirrorCS", {"start": v(7.78, 10.95) * mm, "end": v(9.37, 10.95) * mm});
            skSolve(sketch);
        }
        {
            var Q0;
            Q0 = qSketchRegion(id + "F31", true);
            extrude(context, id + "F32", {"entities" : qUnion([Q0]), "operationType" : NewBodyOperationType.REMOVE, "oppositeDirection" : true, "depth" : 25.4 * mm, "offsetDistance" : 25.4 * mm});
        }
        {
            var Q0;
            Q0 = qSketchRegion(id + "F31", true);
            extrude(context, id + "F33", {"entities" : qUnion([Q0]), "operationType" : NewBodyOperationType.REMOVE, "depth" : 25.4 * mm, "offsetDistance" : 25.4 * mm});
        }
        {
            var Q0;
            Q0 = qSketchRegion(id + "F31", true);
            extrude(context, id + "F34", {"entities" : qUnion([Q0]), "operationType" : NewBodyOperationType.REMOVE, "depth" : 25.4 * mm, "offsetDistance" : 25.4 * mm});
        }
        {
            var Q0;
            Q0 = qSketchRegion(id + "F31", true);
            extrude(context, id + "F35", {"entities" : qUnion([Q0]), "operationType" : NewBodyOperationType.REMOVE, "depth" : 50.8 * mm, "offsetDistance" : 25.4 * mm});
        }
        {
            var Q0;
            Q0=makeQuery(id+"F20.opExtrude","CAP_FACE",FACE,{"disambiguationData":[OSD([sQuery(id+"F19.wireOp",EDGE,"E54.bottom"),sQuery(id+"F19.wireOp",EDGE,"E54.left"),sQuery(id+"F19.wireOp",EDGE,"E54.right"),sQuery(id+"F19.wireOp",EDGE,"E55.bottom"),sQuery(id+"F19.wireOp",EDGE,"E55.top"),sQuery(id+"F19.wireOp",EDGE,"E55.left"),sQuery(id+"F19.wireOp",EDGE,"E56.bottom"),sQuery(id+"F19.wireOp",EDGE,"E56.top"),sQuery(id+"F19.wireOp",EDGE,"E56.left"),sQuery(id+"F19.wireOp",EDGE,"E56.right"),sQuery(id+"F19.wireOp",EDGE,"E57.0.0"),sQuery(id+"F19.wireOp",EDGE,"E57.0.1"),sQuery(id+"F19.wireOp",EDGE,"E57.0.2"),sQuery(id+"F19.wireOp",EDGE,"E57.0.3"),sQuery(id+"F19.wireOp",EDGE,"E58.1.0.0"),sQuery(id+"F19.wireOp",EDGE,"E58.1.0.1"),sQuery(id+"F19.wireOp",EDGE,"E58.1.0.2"),sQuery(id+"F19.wireOp",EDGE,"E58.1.0.3"),sQuery(id+"F19.wireOp",EDGE,"E58.1.0.4"),sQuery(id+"F19.wireOp",EDGE,"E58.1.0.6"),sQuery(id+"F19.wireOp",EDGE,"E58.1.0.7"),sQuery(id+"F19.wireOp",EDGE,"E58.1.0.8"),sQuery(id+"F19.wireOp",EDGE,"E58.1.0.9"),sQuery(id+"F19.wireOp",EDGE,"E58.1.0.10"),sQuery(id+"F19.wireOp",EDGE,"E58.1.0.11")])],"isStart":true});
            var sketch = newSketch(context, id + "F36", { "sketchPlane" : qUnion([Q0])});
            skLineSegment(sketch, "E82", {"start": v(-4.6, 10.56) * mm, "end": v(0, 10.56) * mm});
            skLineSegment(sketch, "E83", {"start": v(-4.6, 10.56) * mm, "end": v(-4.6, 20.22) * mm, "construction": true});
            skLineSegment(sketch, "E84", {"start": v(-4.6, 10.56) * mm, "end": v(-4.6, 4.27) * mm});
            skLineSegment(sketch, "E85", {"start": v(-4.6, 4.27) * mm, "end": v(0, 4.27) * mm});
            skLineSegment(sketch, "E86", {"start": v(-2.22, 8.97) * mm, "end": v(-2.22, 2.42) * mm, "construction": true});
            skCircle(sketch, "E87", {"center": v(-2.22, 6.65) * mm, "radius": 0.8 * mm});
            skPoint(sketch, "E88", {"position": v(0, 21.02) * mm});
            skLineSegment(sketch, "E89", {"start": v(0, 21.02) * mm, "end": v(-0.76, 21.02) * mm});
            skLineSegment(sketch, "E90", {"start": v(-0.76, 21.02) * mm, "end": v(-0.76, 19.5) * mm});
            skLineSegment(sketch, "E91", {"start": v(-0.76, 19.5) * mm, "end": v(-2.29, 19.5) * mm});
            skLineSegment(sketch, "E92", {"start": v(-2.29, 19.5) * mm, "end": v(-2.29, 17.97) * mm});
            skLineSegment(sketch, "E93", {"start": v(-2.29, 17.97) * mm, "end": v(-0.76, 17.97) * mm});
            skLineSegment(sketch, "E94", {"start": v(-0.76, 17.97) * mm, "end": v(-0.76, 17) * mm});
            skLineSegment(sketch, "E95", {"start": v(-0.76, 17) * mm, "end": v(-2.86, 14.9) * mm});
            skLineSegment(sketch, "E96", {"start": v(-2.86, 14.9) * mm, "end": v(-1.9, 13.25) * mm});
            skLineSegment(sketch, "E97", {"start": v(-1.9, 13.25) * mm, "end": v(-4.6, 10.56) * mm});
            skLineSegment(sketch, "E98.MirrorCS", {"start": v(0.76, 17.97) * mm, "end": v(0.76, 17) * mm});
            skLineSegment(sketch, "E99.MirrorCS", {"start": v(0, 21.02) * mm, "end": v(0.76, 21.02) * mm});
            skLineSegment(sketch, "E100.MirrorCS", {"start": v(4.6, 10.56) * mm, "end": v(4.6, 20.22) * mm, "construction": true});
            skLineSegment(sketch, "E101.MirrorCS", {"start": v(2.22, 8.97) * mm, "end": v(2.22, 2.42) * mm, "construction": true});
            skLineSegment(sketch, "E102.MirrorCS", {"start": v(2.29, 17.97) * mm, "end": v(0.76, 17.97) * mm});
            skLineSegment(sketch, "E103.MirrorCS", {"start": v(0.76, 17) * mm, "end": v(2.86, 14.9) * mm});
            skLineSegment(sketch, "E104.MirrorCS", {"start": v(2.29, 19.5) * mm, "end": v(2.29, 17.97) * mm});
            skLineSegment(sketch, "E105.MirrorCS", {"start": v(0.76, 21.02) * mm, "end": v(0.76, 19.5) * mm});
            skLineSegment(sketch, "E106.MirrorCS", {"start": v(4.6, 10.56) * mm, "end": v(4.6, 4.27) * mm});
            skLineSegment(sketch, "E107.MirrorCS", {"start": v(1.9, 13.25) * mm, "end": v(4.6, 10.56) * mm});
            skLineSegment(sketch, "E108.MirrorCS", {"start": v(4.6, 10.56) * mm, "end": v(0, 10.56) * mm});
            skLineSegment(sketch, "E109.MirrorCS", {"start": v(2.86, 14.9) * mm, "end": v(1.9, 13.25) * mm});
            skLineSegment(sketch, "E110.MirrorCS", {"start": v(4.6, 4.27) * mm, "end": v(0, 4.27) * mm});
            skLineSegment(sketch, "E111.MirrorCS", {"start": v(0.76, 19.5) * mm, "end": v(2.29, 19.5) * mm});
            skCircle(sketch, "E112.MirrorC", {"center": v(3.81, 6.65) * mm, "radius": 0.8 * mm});
            skLineSegment(sketch, "E113", {"start": v(4.6, 10.56) * mm, "end": v(6.2, 8.97) * mm});
            skLineSegment(sketch, "E114", {"start": v(6.2, 8.97) * mm, "end": v(6.2, 4.27) * mm});
            skLineSegment(sketch, "E115", {"start": v(6.2, 4.27) * mm, "end": v(4.6, 4.27) * mm});
            skLineSegment(sketch, "E116", {"start": v(-2.22, 6.65) * mm, "end": v(-4.6, 6.65) * mm, "construction": true});
            skLineSegment(sketch, "E117", {"start": v(3.81, 6.65) * mm, "end": v(6.2, 6.65) * mm, "construction": true});
            skSolve(sketch);
        }
        {
            var Q0;
            Q0 = qSketchRegion(id + "F36", true);
            extrude(context, id + "F37", {"entities" : qUnion([Q0]), "depth" : (getVariable(context, 'h')) * mm, "offsetDistance" : 25.4 * mm});
        }
        {
            var Q0;
            Q0=makeQuery(id+"F37.opExtrude","CAP_FACE",FACE,{"disambiguationData":[OSD([sQuery(id+"F36.wireOp",EDGE,"E84"),sQuery(id+"F36.wireOp",EDGE,"E85"),sQuery(id+"F36.wireOp",EDGE,"E89"),sQuery(id+"F36.wireOp",EDGE,"E90"),sQuery(id+"F36.wireOp",EDGE,"E91"),sQuery(id+"F36.wireOp",EDGE,"E92"),sQuery(id+"F36.wireOp",EDGE,"E93"),sQuery(id+"F36.wireOp",EDGE,"E94"),sQuery(id+"F36.wireOp",EDGE,"E95"),sQuery(id+"F36.wireOp",EDGE,"E96"),sQuery(id+"F36.wireOp",EDGE,"E97"),sQuery(id+"F36.wireOp",EDGE,"E98.MirrorCS"),sQuery(id+"F36.wireOp",EDGE,"E99.MirrorCS"),sQuery(id+"F36.wireOp",EDGE,"E102.MirrorCS"),sQuery(id+"F36.wireOp",EDGE,"E103.MirrorCS"),sQuery(id+"F36.wireOp",EDGE,"E104.MirrorCS"),sQuery(id+"F36.wireOp",EDGE,"E105.MirrorCS"),sQuery(id+"F36.wireOp",EDGE,"E107.MirrorCS"),sQuery(id+"F36.wireOp",EDGE,"E109.MirrorCS"),sQuery(id+"F36.wireOp",EDGE,"E110.MirrorCS"),sQuery(id+"F36.wireOp",EDGE,"E111.MirrorCS"),sQuery(id+"F36.wireOp",EDGE,"E112.MirrorC"),sQuery(id+"F36.wireOp",EDGE,"E113"),sQuery(id+"F36.wireOp",EDGE,"E114"),sQuery(id+"F36.wireOp",EDGE,"E115")])],"isStart":false});
            var sketch = newSketch(context, id + "F38", { "sketchPlane" : qUnion([Q0])});
            skCircle(sketch, "E118.0", {"center": v(-2.22, 6.65) * mm, "radius": 0.8 * mm});
            skSolve(sketch);
        }
        {
            var Q0;
            Q0=makeQuery(id+"F38.imprint","IMPRINT",FACE,{"disambiguationData":[TD([[makeQuery(id+"F38.imprint","IMPRINT",EDGE,{"derivedFrom":sQuery(id+"F38.wireOp",EDGE,"E118.0")}),1.0]])]});
            extrude(context, id + "F39", {"entities" : qUnion([Q0]), "operationType" : NewBodyOperationType.REMOVE, "oppositeDirection" : true, "depth" : 25.4 * mm, "offsetDistance" : 25.4 * mm});
        }
    });
